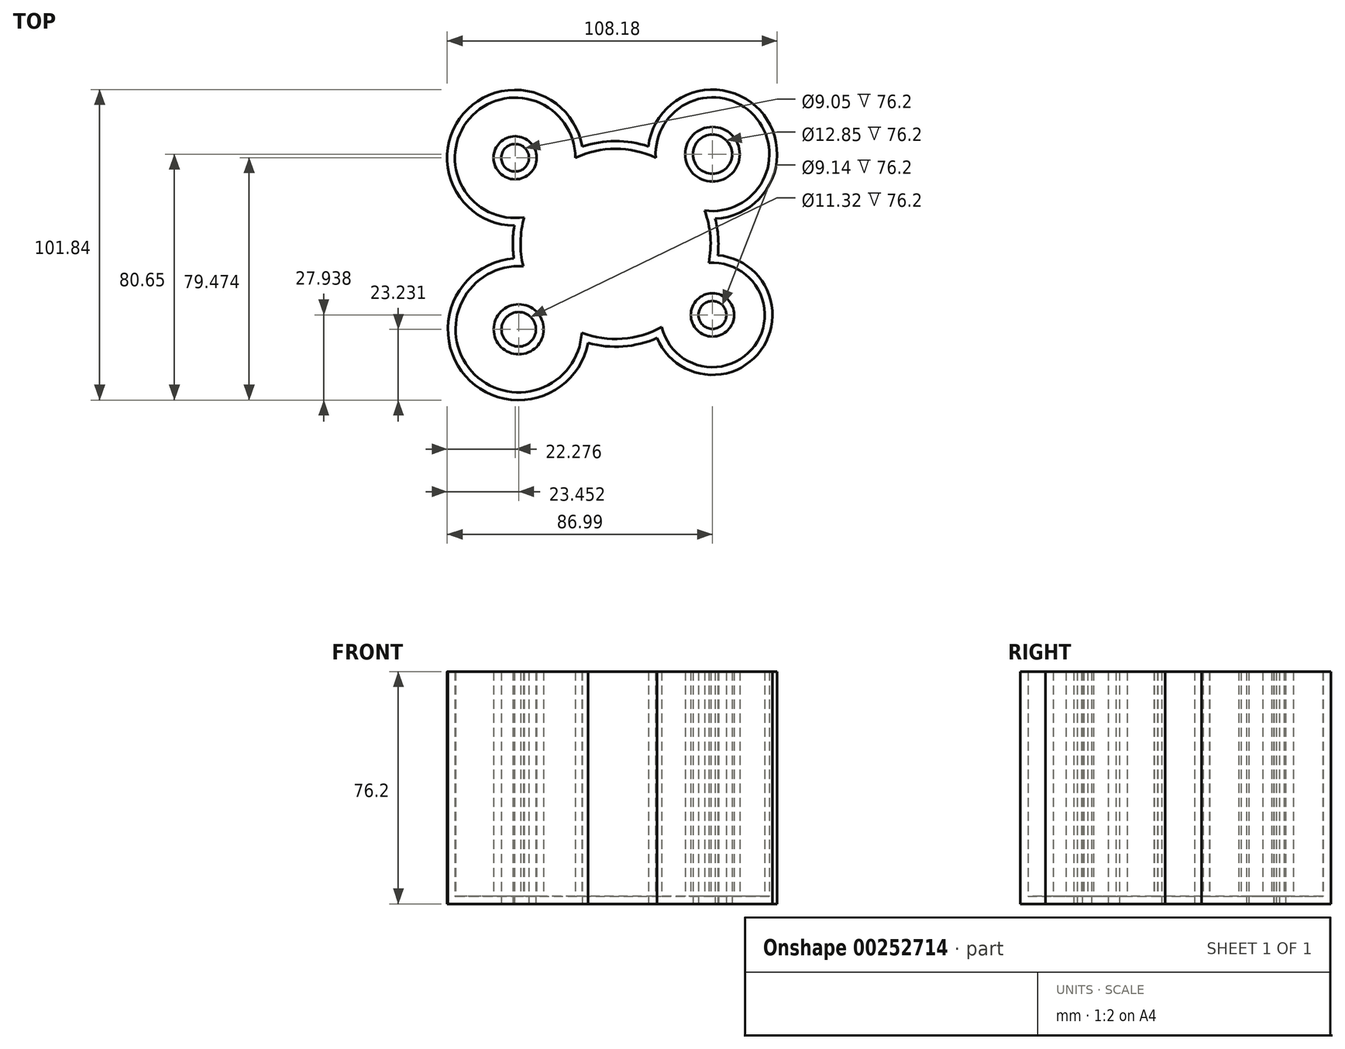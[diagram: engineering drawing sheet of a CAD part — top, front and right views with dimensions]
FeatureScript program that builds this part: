
annotation { "Feature Type Name" : "Feature", "Feature Type Description" : "" }
export const myFeature = defineFeature(function(context is Context, id is Id, definition is map)
    precondition{}
    {
        {
            var Q0;
            Q0=qCreatedBy(makeId("Top.planeOp"),FACE);
            var sketch = newSketch(context, id + "F0", { "sketchPlane" : qUnion([Q0])});
            skArc(sketch, "E0", {"start": v(-39.77, 13.26) * mm, "mid": v(-40.3, 7.87) * mm, "end": v(-39.96, 2.47) * mm});
            skArc(sketch, "E1", {"start": v(7.02, -23.55) * mm, "mid": v(41.04, -27.63) * mm, "end": v(26.92, 3.59) * mm});
            skArc(sketch, "E2", {"start": v(-17.56, 39.18) * mm, "mid": v(-56.45, 50.03) * mm, "end": v(-39.77, 13.26) * mm});
            skArc(sketch, "E3", {"start": v(26.1, 15.54) * mm, "mid": v(40.72, 51.1) * mm, "end": v(4.15, 39.25) * mm});
            skArc(sketch, "E4", {"start": v(-39.96, 2.47) * mm, "mid": v(-55.78, -36.07) * mm, "end": v(-15.57, -25.2) * mm});
            skArc(sketch, "E5.trimOffspring", {"start": v(-15.57, -25.2) * mm, "mid": v(-4.13, -26.33) * mm, "end": v(7.02, -23.55) * mm});
            skArc(sketch, "E6.trimOffspring", {"start": v(26.92, 3.59) * mm, "mid": v(27.05, 9.6) * mm, "end": v(26.1, 15.54) * mm});
            skArc(sketch, "E7.trimOffspring", {"start": v(4.15, 39.25) * mm, "mid": v(-6.71, 41) * mm, "end": v(-17.56, 39.18) * mm});
            skCircle(sketch, "E8", {"center": v(-39.53, 35.53) * mm, "radius": 4.53 * mm});
            skCircle(sketch, "E9", {"center": v(25.18, 36.71) * mm, "radius": 6.42 * mm});
            skCircle(sketch, "E10", {"center": v(25.18, -16) * mm, "radius": 4.57 * mm});
            skCircle(sketch, "E11", {"center": v(-38.36, -20.7) * mm, "radius": 5.66 * mm});
            skSolve(sketch);
        }
        {
            var Q0;
            Q0 = qSketchRegion(id + "F0", true);
            extrude(context, id + "F1", {"entities" : qUnion([Q0]), "depth" : 76.2 * mm});
        }
        {
            var Q0;
            Q0=makeQuery(id+"F1.opExtrude","CAP_FACE",FACE,{"disambiguationData":[OSD([sQuery(id+"F0.wireOp",EDGE,"E0"),sQuery(id+"F0.wireOp",EDGE,"E1"),sQuery(id+"F0.wireOp",EDGE,"E2"),sQuery(id+"F0.wireOp",EDGE,"E3"),sQuery(id+"F0.wireOp",EDGE,"E4"),sQuery(id+"F0.wireOp",EDGE,"E5.trimOffspring"),sQuery(id+"F0.wireOp",EDGE,"E6.trimOffspring"),sQuery(id+"F0.wireOp",EDGE,"E7.trimOffspring")])],"isStart":false});
            shell(context, id + "F2", {"entities" : qUnion([Q0]), "thickness" : 2.54 * mm});
        }
    });
